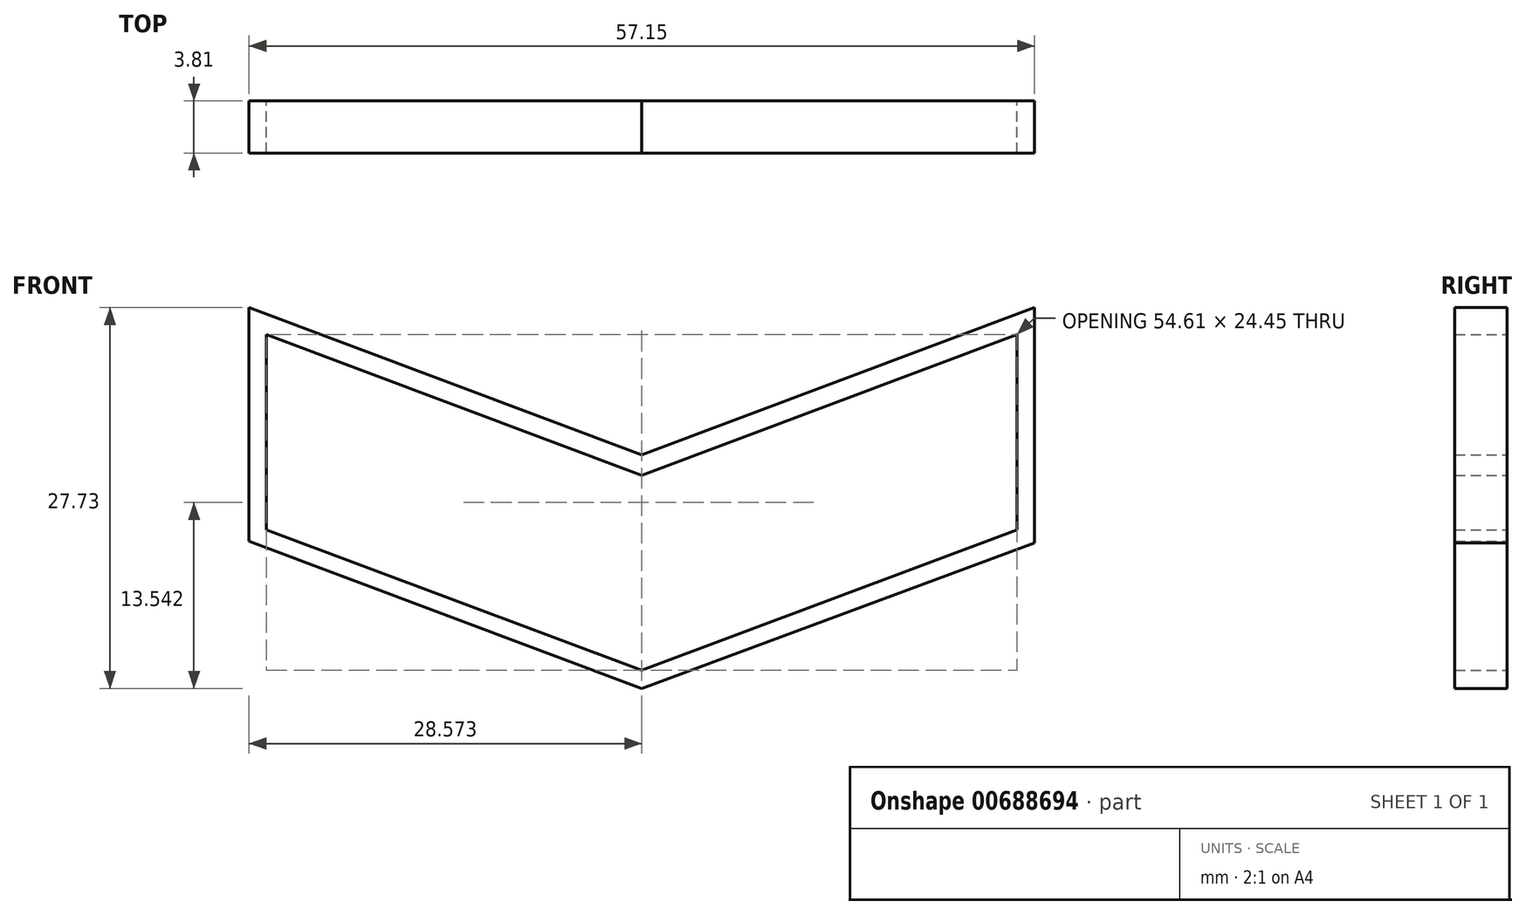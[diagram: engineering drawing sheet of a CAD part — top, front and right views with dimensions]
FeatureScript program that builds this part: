
annotation { "Feature Type Name" : "Feature", "Feature Type Description" : "" }
export const myFeature = defineFeature(function(context is Context, id is Id, definition is map)
    precondition{}
    {
        {
            var Q0;
            Q0=qCreatedBy(makeId("Front.planeOp"),FACE);
            var sketch = newSketch(context, id + "F0", { "sketchPlane" : qUnion([Q0])});
            skLineSegment(sketch, "E0", {"start": v(-0.14, 4.82) * mm, "end": v(-27.44, 15.06) * mm});
            skLineSegment(sketch, "E1", {"start": v(-27.44, 15.06) * mm, "end": v(-27.44, 0.84) * mm});
            skLineSegment(sketch, "E2", {"start": v(-27.44, 0.84) * mm, "end": v(-0.14, -9.4) * mm});
            skLineSegment(sketch, "E3.MirrorCS", {"start": v(27.17, 0.84) * mm, "end": v(-0.14, -9.4) * mm});
            skLineSegment(sketch, "E4.MirrorCS", {"start": v(27.17, 15.06) * mm, "end": v(27.17, 0.84) * mm});
            skLineSegment(sketch, "E5.MirrorCS", {"start": v(-0.14, 4.82) * mm, "end": v(27.17, 15.06) * mm});
            skLineSegment(sketch, "E6", {"start": v(-0.14, 6.3) * mm, "end": v(28.44, 17.02) * mm});
            skLineSegment(sketch, "E7", {"start": v(28.44, 17.02) * mm, "end": v(28.44, -0.12) * mm});
            skLineSegment(sketch, "E8", {"start": v(28.44, -0.12) * mm, "end": v(-0.14, -10.71) * mm});
            skLineSegment(sketch, "E9", {"start": v(-0.14, -10.71) * mm, "end": v(-28.71, 0) * mm});
            skLineSegment(sketch, "E10", {"start": v(-28.71, 0) * mm, "end": v(-28.71, 17.06) * mm});
            skLineSegment(sketch, "E11", {"start": v(-0.14, 6.3) * mm, "end": v(-28.71, 17.02) * mm});
            skSolve(sketch);
        }
        {
            var Q0;
            Q0 = qSketchRegion(id + "F0", true);
            extrude(context, id + "F1", {"entities" : qUnion([Q0]), "depth" : 3.8 * mm, "offsetDistance" : 25.4 * mm});
        }
    });
